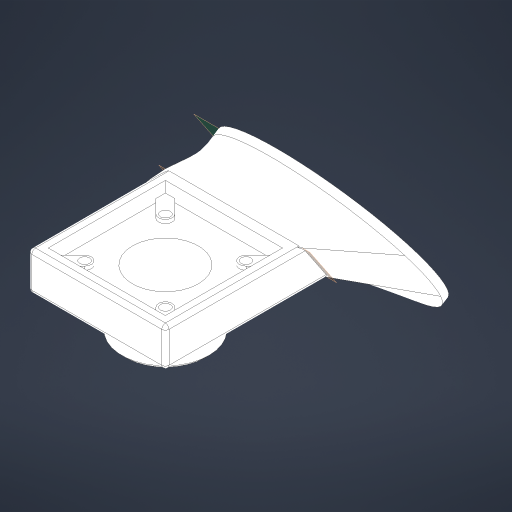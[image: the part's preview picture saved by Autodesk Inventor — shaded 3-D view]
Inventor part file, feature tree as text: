
AUTODESK INVENTOR PART (.ipt)
format: ipt  version: 2023 (Build 270158000, 158)  size: 443,904 bytes
history: native  units: in
note: dims shown in document units (in); Inventor stores cm internally (conversion verified against a paired STEP export)
features: sketch x9, extrude x6, hole x3, plane x2, fillet x2, projected_geometry x2, other x2, loft x1, chamfer x1
ambient origin geometry x8: Origin, YZ Plane, XZ Plane, XY Plane, X Axis, Y Axis, Z Axis, Center Point
bodies: Solid1 (feature_tree)
feature tree (28):
  extrude  "Extrusion1"  Depth=0.525in
  extrude  "Extrusion2"  Depth=0.3848in
  plane  "Work Plane1"
  extrude  "Extrusion3"  Depth=0.6in
  loft  "Loft1"
  extrude  "Extrusion4"  Depth=0.2in TaperAngle=0.0deg
  hole  "Hole1"  [1 undecoded]
  extrude  "Extrusion5"  Depth=0.5in
  extrude  "Extrusion6"  Depth=0.05in TaperAngle=0.0deg
  hole  "Hole2"  [1 undecoded]
  plane  "Work Plane2"
  hole  "Hole3"  [1 undecoded]
  fillet  "Fillet1"  [1 undecoded]
  chamfer  "Chamfer1"  Distance=0.4in
  fillet  "Fillet2"  Radius=0.25in
  sketch  "Sketch1"  dims[d0=1.875in d1=0.525in]
  sketch  "Sketch2"  dims[d2=1.875in d3=0.0in d4=0.3848in]
  sketch  "Sketch3"  dims[d5=1.875in d6=0.0in d7=0.6in]
  sketch  "Sketch4"  dims[d10=0.1in d11=0.0in d14=0.0in d15=90.0deg]
  projected_geometry  "Projected Loop1"
  sketch  "Sketch5"  dims[d16=1.6in d17=0.2in d18=0.0in]
  sketch  "Sketch6"  dims[d19=0.9in d20=0.75in d21=0.119in d22=0.25in d23=0.6871in d24=1.0in d25=0.8108in d26=1.1875in]
  sketch  "Sketch7"  dims[d27=0.5in d28=0.0in d29=0.1839in]
  projected_geometry  "Projected Loop2"
  sketch  "Sketch8"  dims[d30=1.1024in d31=0.05in d32=0.0in]
  sketch  "Sketch9"  dims[d33=0.1339in d34=0.75in d35=0.185in d36=0.25in d37=0.6871in d38=1.0in d39=0.8108in d40=0.9792in d41=0.9792in d42=30.0deg d43=0.4in d44=0.25in d45=0.177in d46=0.75in d47=0.313in d48=0.45in d49=0.5635in d50=1.0in d51=0.8108in d52=0.05in d53=0.05in d54=0.125in d55=45.0deg d56=0.0625in d57=2.75in d58=0.0in d59=90.0deg]
  other  "Edges2"
  other  "Edges3"
note: 4 required parameter values undecoded (feature->parameter linkage not recoverable at this tier; creation-order binding heuristic only, values carry confidence <= 0.55)
